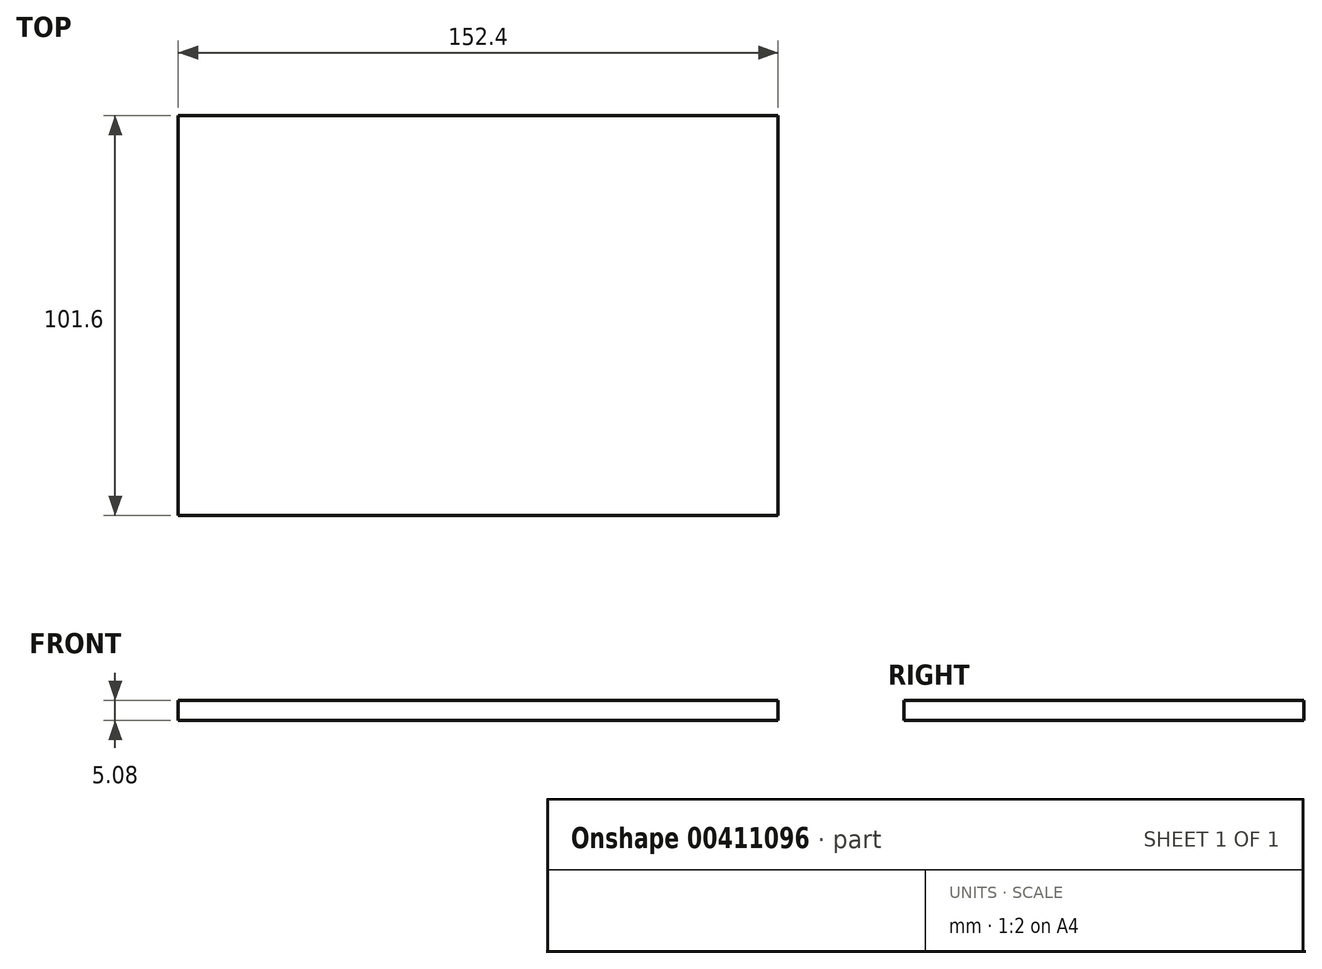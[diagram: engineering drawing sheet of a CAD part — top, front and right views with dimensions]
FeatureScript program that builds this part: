
annotation { "Feature Type Name" : "Feature", "Feature Type Description" : "" }
export const myFeature = defineFeature(function(context is Context, id is Id, definition is map)
    precondition{}
    {
        {
            var Q0;
            Q0=qCreatedBy(makeId("Top.planeOp"), FACE);
            var sketch = newSketch(context, id + "F0", { "sketchPlane" : qUnion([Q0])});
            skLineSegment(sketch, "E0.bottom", {"start": v(76.2, 50.8) * mm, "end": v(-76.2, 50.8) * mm});
            skLineSegment(sketch, "E0.top", {"start": v(76.2, -50.8) * mm, "end": v(-76.2, -50.8) * mm});
            skLineSegment(sketch, "E0.left", {"start": v(76.2, 50.8) * mm, "end": v(76.2, -50.8) * mm});
            skLineSegment(sketch, "E0.right", {"start": v(-76.2, 50.8) * mm, "end": v(-76.2, -50.8) * mm});
            skPoint(sketch, "E0.middle", {"position": v(0, 0) * mm});
            skSolve(sketch);
        }
        {
            var Q0;
            Q0 = qSketchRegion(id + "F0", true);
            extrude(context, id + "F1", {"entities" : qUnion([Q0]), "domain" : OperationDomain.MODEL, "flatOperationType" : FlatOperationType.REMOVE, "depth" : 5.08 * mm, "offsetDistance" : 25.4 * mm});
        }
    });
